# Revit family: Betonsteinpflaster
name_source: partatom
category: Allgemeines Modell
revit_build: Autodesk Revit 2016 (Build: 20161004_0715(x64)
units: mm (PartAtom-declared; Revit-internal decimal feet)

## family parameters
Arbeitsebenenbasiert = Nein
Beim Laden mit Abzugskörper schneiden = Nein
Bemaßung runder Anschluss = Durchmesser verwenden
Gemeinsam genutzt = Nein
Immer vertikal = Ja
Kann Basisbauteil für Bewehrung sein = Nein
Raumberechnungspunkt = Nein
Teiletyp = Normal

## types (4) — shared parameters
Fasenausbildung = Minifase
Hersteller = Kronimus AG, Iffezheim
Material = Natursteinvorsatz + Hinterbeton (zweischichtig)
Norm = DIN EN 12878
Produktfamilie = Betonsteinpflaster
Produktionsnorm = DIN EN 1338
Produktname = Großpflaster
Produzent = Kronimus AG, Iffezheim
Steinlänge = 300 mm
verfügbare Steindicke in mm = 80
www = www.kronimus.de

## per-type parameters (varying)
| type | Artikelnummer | Farbausführung | GTIN - Nummer | LRV-Wert | Materialität | Oberflächenbearbeitung | R-Wert  nach DIN 51130 | Rastermaß L/ B in mm | Stations-Kategorie | Steinbreite |
| Großpflaster 300/150  3-5 Anthrazit gesprenkelt | 2-351508-275-07 | Nr. 275 DB Anthrazit gesprenkelt | 4060851016892 | 10,63 | Nr. 275 DB Anthrazit gesprenkelt | geschliffen | R11 | 300/150 | 3-5 | 150 mm |
| Großpflaster 300/300  3-5 Anthrazit gesprenkelt | 2-353008-275-07 | Nr. 275 DB Anthrazit gesprenkelt | 4060851016885 | 10,63 | Nr. 275 DB Anthrazit gesprenkelt | geschliffen | R12 | 300/300 | 3-5 | 300 mm |
| Großpflaster 300/150  6-7 Anthrazit dunkel | 2-351508-269-00 | Nr. 269 DB Anthrazit dunkel | 4060851016878 | 6,64 | Nr. 269 DB Anthrazit dunkel | eingefärbt | R12 | 300/150 | 6-7 | 150 mm |
| Großpflaster 300/300  6-7 Anthrazit dunkel | 2-353008-269-00 | Nr. 269 DB Anthrazit dunkel | 4060851016861 | 6,64 | Nr. 269 DB Anthrazit dunkel | eingefärbt | R12 | 300/300 | 6-7 | 300 mm |
